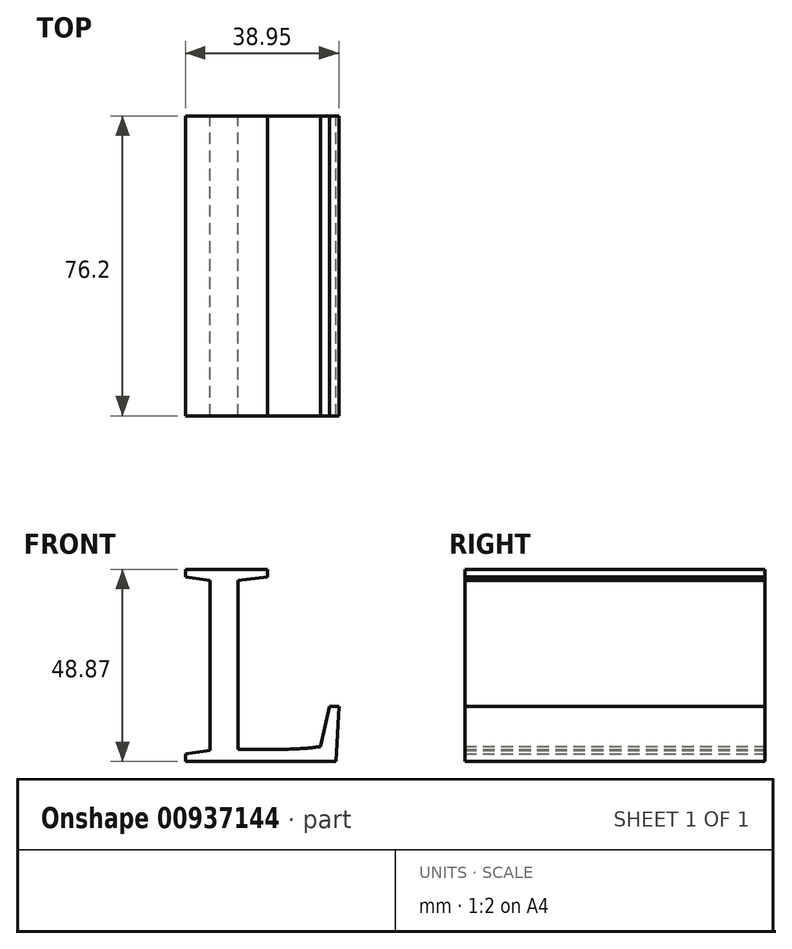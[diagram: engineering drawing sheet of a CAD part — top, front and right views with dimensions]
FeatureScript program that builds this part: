
annotation { "Feature Type Name" : "Feature", "Feature Type Description" : "" }
export const myFeature = defineFeature(function(context is Context, id is Id, definition is map)
    precondition{}
    {
        {
            var Q0;
            Q0=qCreatedBy(makeId("Front.planeOp"),FACE);
            var sketch = newSketch(context, id + "F0", { "sketchPlane" : qUnion([Q0])});
            skText(sketch, "E0", { "text": "L", "fontName": "Tinos-Regular.ttf"});
            const initialGuessF0  = {"E0": [-0.04577, 0, 1, 0, 0.05373]};
            skSetInitialGuess(sketch, initialGuessF0);
            skSolve(sketch);
        }
        {
            var Q0;
            Q0=makeQuery(id+"F0.imprint","IMPRINT",FACE,{"disambiguationData":[TD([[makeQuery(id+"F0.imprint","IMPRINT",EDGE,{"derivedFrom":sQuery(id+"F0.wireOp",EDGE,"E0.sketch_text.stroke-0")}),-1.0]])]});
            extrude(context, id + "F1", {"entities" : qUnion([Q0]), "depth" : 76.2 * mm, "offsetDistance" : 25.4 * mm, "symmetric" : true});
        }
    });
